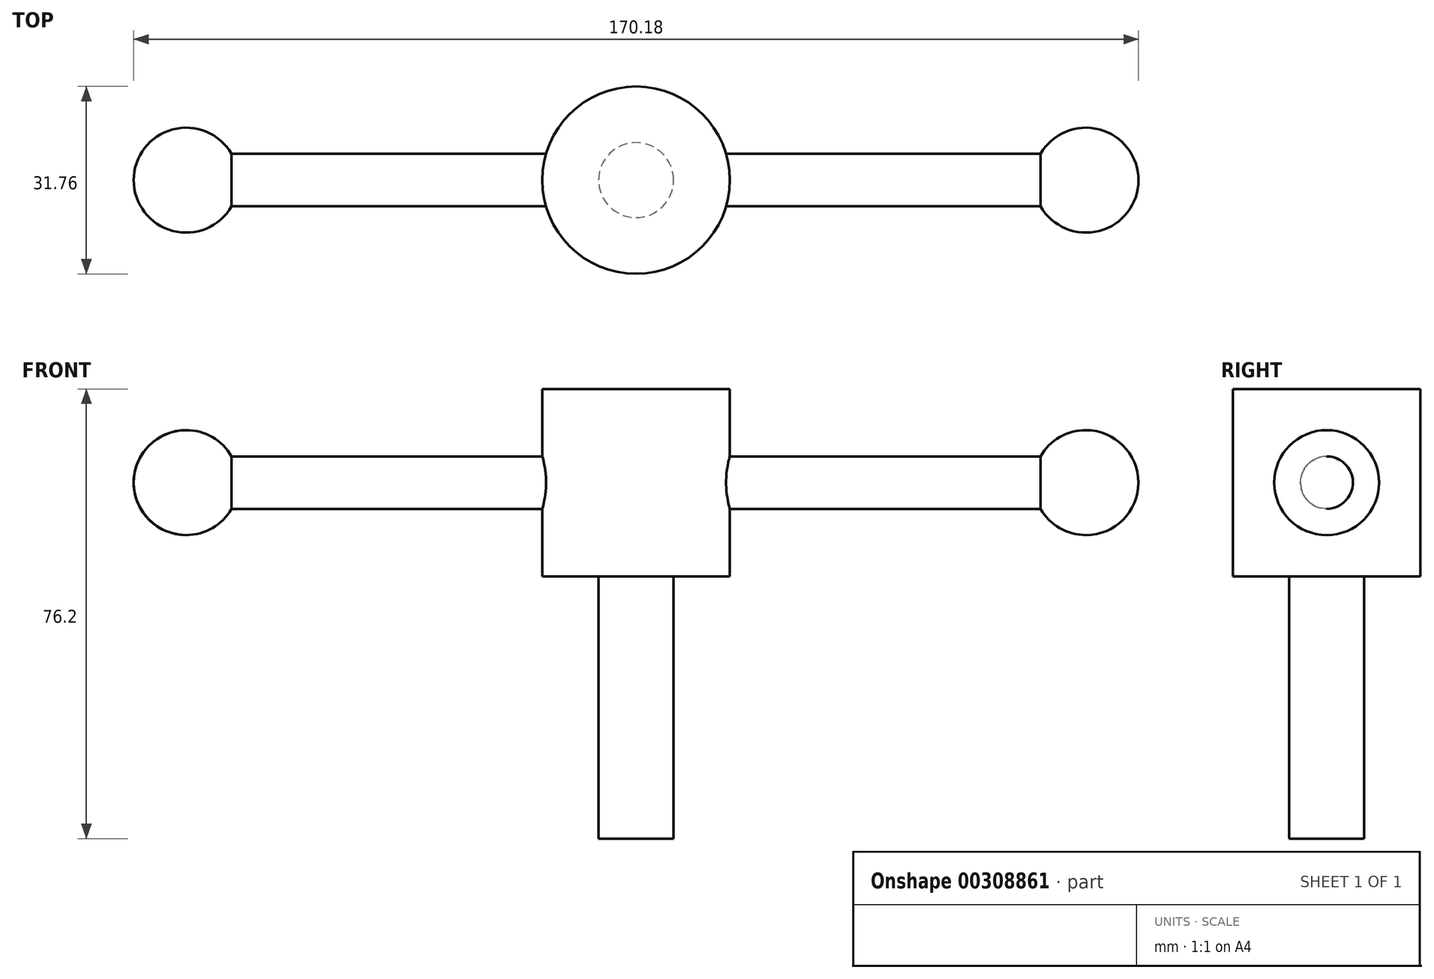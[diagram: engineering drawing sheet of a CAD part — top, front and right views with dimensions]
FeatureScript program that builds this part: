
annotation { "Feature Type Name" : "Feature", "Feature Type Description" : "" }
export const myFeature = defineFeature(function(context is Context, id is Id, definition is map)
    precondition{}
    {
        {
            var Q0;
            Q0=qCreatedBy(makeId("Top.planeOp"),FACE);
            var sketch = newSketch(context, id + "F0", { "sketchPlane" : qUnion([Q0])});
            skCircle(sketch, "E0", {"center": v(0, 0) * mm, "radius": 15.88 * mm});
            skSolve(sketch);
        }
        {
            var Q0;
            Q0 = qSketchRegion(id + "F0", true);
            extrude(context, id + "F1", {"entities" : qUnion([Q0]), "depth" : 76.2 * mm});
        }
        {
            var Q0;
            Q0=qCreatedBy(makeId("Top.planeOp"),FACE);
            var sketch = newSketch(context, id + "F2", { "sketchPlane" : qUnion([Q0])});
            skCircle(sketch, "E1", {"center": v(0, 0) * mm, "radius": 6.35 * mm});
            skCircle(sketch, "E2", {"center": v(0, 0) * mm, "radius": 15.88 * mm});
            skSolve(sketch);
        }
        {
            var Q0;
            Q0 = qSketchRegion(id + "F2", true);
            extrude(context, id + "F3", {"entities" : qUnion([Q0]), "operationType" : NewBodyOperationType.REMOVE, "depth" : 44.45 * mm});
        }
        {
            var Q0;
            Q0=qCreatedBy(makeId("Right.planeOp"),FACE);
            var sketch = newSketch(context, id + "F4", { "sketchPlane" : qUnion([Q0])});
            skCircle(sketch, "E3", {"center": v(0, 60.33) * mm, "radius": 4.45 * mm});
            skSolve(sketch);
        }
        {
            var Q0;
            Q0 = qSketchRegion(id + "F4", true);
            extrude(context, id + "F5", {"entities" : qUnion([Q0]), "operationType" : NewBodyOperationType.ADD, "endBound" : BoundingType.SYMMETRIC, "depth" : 152.4 * mm});
        }
        {
            var Q0;
            Q0=makeQuery(id+"F5.opExtrude","CAP_FACE",FACE,{"disambiguationData":[OSD([sQuery(id+"F4.wireOp",EDGE,"E3")])],"isStart":false});
            var sketch = newSketch(context, id + "F6", { "sketchPlane" : qUnion([Q0])});
            skCircle(sketch, "E4", {"center": v(0, 60.33) * mm, "radius": 4.44 * mm});
            skSolve(sketch);
        }
        {
            var Q0;
            Q0=qCreatedBy(makeId("Front.planeOp"),FACE);
            var sketch = newSketch(context, id + "F7", { "sketchPlane" : qUnion([Q0])});
            skArc(sketch, "E5", {"start": v(76.2, 51.44) * mm, "mid": v(67.31, 60.33) * mm, "end": v(76.2, 69.22) * mm});
            skLineSegment(sketch, "E6", {"start": v(76.2, 69.22) * mm, "end": v(76.2, 51.44) * mm});
            skArc(sketch, "E7", {"start": v(76.2, 69.22) * mm, "mid": v(85.1, 60.33) * mm, "end": v(76.2, 51.44) * mm});
            skSolve(sketch);
        }
        {
            var Q0;
            Q0=makeQuery(id+"F7.imprint","IMPRINT",FACE,{"disambiguationData":[TD([[makeQuery(id+"F7.imprint","IMPRINT",EDGE,{"derivedFrom":sQuery(id+"F7.wireOp",EDGE,"E6")}),1.0]])]});
            var Q1;
            Q1=sQuery(id+"F7.wireOp",EDGE,"E6");
            revolve(context, id + "F8", {"operationType" : NewBodyOperationType.ADD, "entities" : qUnion([Q0]), "axis" : qUnion([Q1]), "revolveType" : RevolveType.TWO_DIRECTIONS, "angle" : 30 * degree, "angleBack" : 30 * degree});
        }
        {
            var Q0;
            Q0=makeQuery(id+"F5.opExtrude","CAP_FACE",FACE,{"disambiguationData":[OSD([sQuery(id+"F4.wireOp",EDGE,"E3")])],"isStart":true});
            var sketch = newSketch(context, id + "F9", { "sketchPlane" : qUnion([Q0])});
            skLineSegment(sketch, "E8", {"start": v(0, 64.77) * mm, "end": v(0, 55.88) * mm, "construction": true});
            skSolve(sketch);
        }
        {
            var Q0;
            Q0=qCreatedBy(makeId("Front.planeOp"),FACE);
            var sketch = newSketch(context, id + "F10", { "sketchPlane" : qUnion([Q0])});
            skLineSegment(sketch, "E9", {"start": v(-76.2, 64.77) * mm, "end": v(-76.2, 55.88) * mm});
            skSolve(sketch);
        }
        {
            var Q0;
            Q0=qCreatedBy(makeId("Front.planeOp"),FACE);
            var sketch = newSketch(context, id + "F11", { "sketchPlane" : qUnion([Q0])});
            skArc(sketch, "E10", {"start": v(-76.2, 69.22) * mm, "mid": v(-85.1, 60.33) * mm, "end": v(-76.2, 51.44) * mm});
            skLineSegment(sketch, "E11", {"start": v(-76.2, 69.22) * mm, "end": v(-76.2, 51.44) * mm});
            skSolve(sketch);
        }
        {
            var Q0;
            Q0 = qSketchRegion(id + "F11", true);
            var Q1;
            Q1=sQuery(id+"F11.wireOp",EDGE,"E11");
            revolve(context, id + "F12", {"operationType" : NewBodyOperationType.ADD, "entities" : qUnion([Q0]), "axis" : qUnion([Q1]), "revolveType" : RevolveType.FULL});
        }
    });
